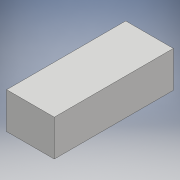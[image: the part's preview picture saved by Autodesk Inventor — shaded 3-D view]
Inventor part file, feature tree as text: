
AUTODESK INVENTOR PART (.ipt)
format: ipt  version: 2017 (Build 210142000, 142)  size: 86,016 bytes
history: native  units: mm
features: other x1, extrude x1, sketch x1
ambient origin geometry x8: Origin, YZ Plane, XZ Plane, XY Plane, X Axis, Y Axis, Z Axis, Center Point
bodies: Body1 (feature_tree)
feature tree (3):
  other  "ソリッド1"
  extrude  "押し出し1"  Depth=0.42mm
  sketch  "スケッチ1"
